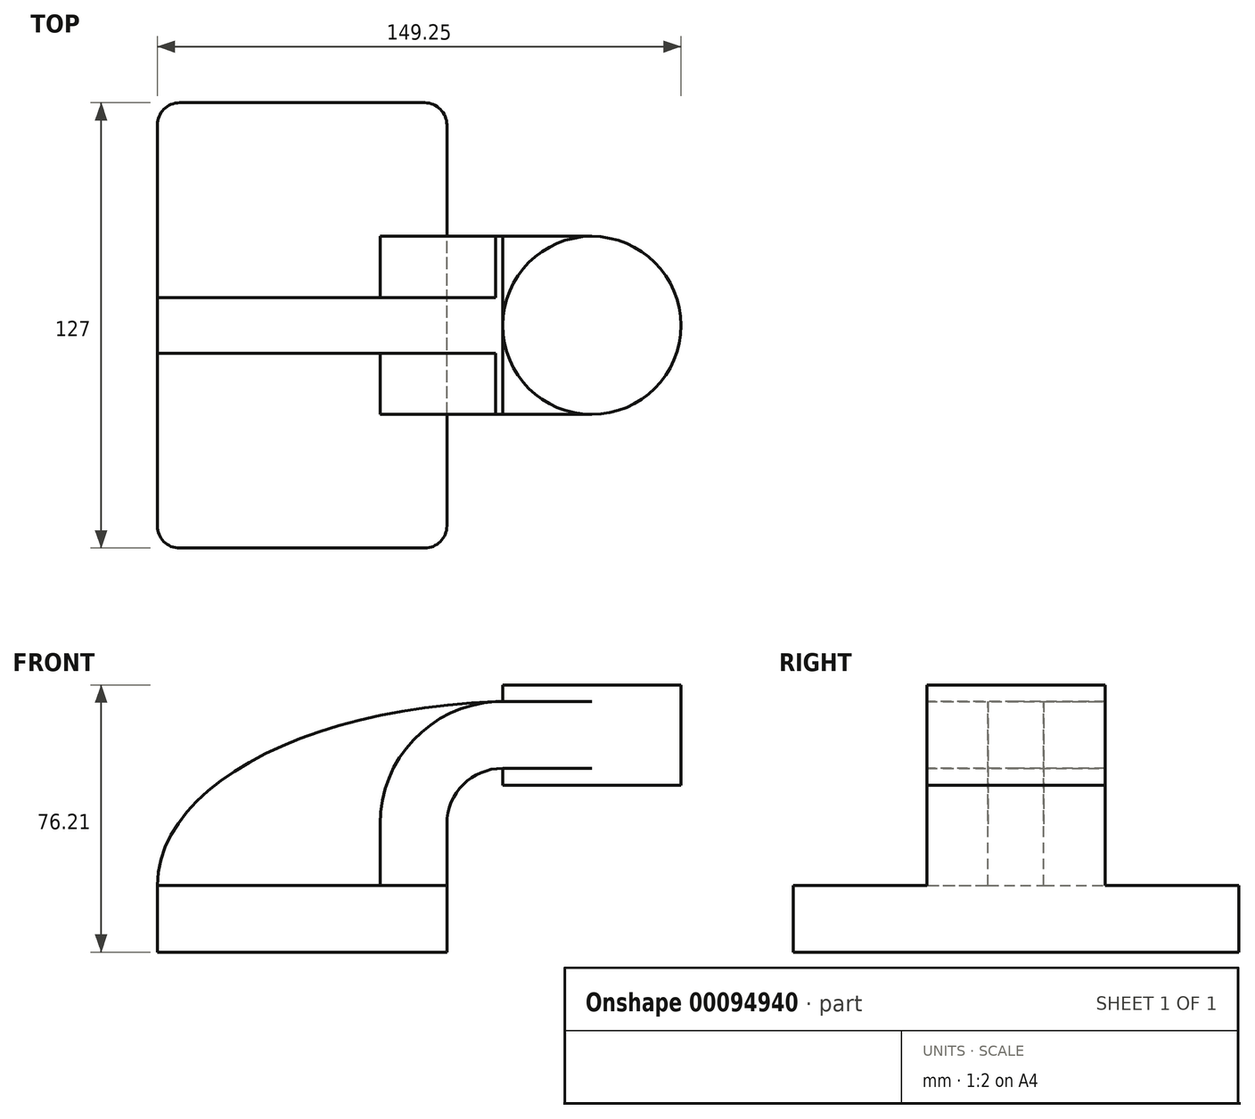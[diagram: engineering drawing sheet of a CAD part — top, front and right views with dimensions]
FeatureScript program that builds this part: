
annotation { "Feature Type Name" : "Feature", "Feature Type Description" : "" }
export const myFeature = defineFeature(function(context is Context, id is Id, definition is map)
    precondition{}
    {
        {
            var Q0;
            Q0=qCreatedBy(makeId("Front.planeOp"),FACE);
            var sketch = newSketch(context, id + "F0", { "sketchPlane" : qUnion([Q0])});
            skLineSegment(sketch, "E0.bottom", {"start": v(41.27, 9.53) * mm, "end": v(-41.28, 9.53) * mm});
            skLineSegment(sketch, "E0.top", {"start": v(41.28, -9.52) * mm, "end": v(-41.27, -9.52) * mm});
            skLineSegment(sketch, "E0.left", {"start": v(41.27, 9.53) * mm, "end": v(41.28, -9.52) * mm});
            skLineSegment(sketch, "E0.right", {"start": v(-41.28, 9.53) * mm, "end": v(-41.27, -9.52) * mm});
            skPoint(sketch, "E0.middle", {"position": v(0, 0) * mm});
            skLineSegment(sketch, "E1.bottom", {"start": v(107.97, 38.1) * mm, "end": v(57.17, 38.1) * mm});
            skLineSegment(sketch, "E1.top", {"start": v(107.97, 66.68) * mm, "end": v(57.17, 66.68) * mm});
            skLineSegment(sketch, "E1.left", {"start": v(107.97, 38.1) * mm, "end": v(107.97, 66.68) * mm});
            skLineSegment(sketch, "E1.right", {"start": v(57.17, 38.1) * mm, "end": v(57.17, 66.68) * mm});
            skPoint(sketch, "E1.middle", {"position": v(82.57, 52.39) * mm});
            skLineSegment(sketch, "E2", {"start": v(41.27, 9.53) * mm, "end": v(41.27, 27) * mm});
            skArc(sketch, "E3", {"start": v(41.27, 27) * mm, "mid": v(45.92, 38.23) * mm, "end": v(57.15, 42.88) * mm});
            skLineSegment(sketch, "E4", {"start": v(57.15, 42.88) * mm, "end": v(82.57, 42.88) * mm});
            skLineSegment(sketch, "E5.0", {"start": v(57.15, 61.93) * mm, "end": v(82.57, 61.93) * mm});
            skArc(sketch, "E5.1", {"start": v(22.22, 27) * mm, "mid": v(32.45, 51.7) * mm, "end": v(57.15, 61.93) * mm});
            skLineSegment(sketch, "E5.2", {"start": v(22.22, 9.53) * mm, "end": v(22.22, 27) * mm});
            skLineSegment(sketch, "E6", {"start": v(82.57, 38.1) * mm, "end": v(82.57, 66.68) * mm});
            skFitSpline(sketch, "E7", {"points": [v(-41.28, 9.53) * mm, v(57.15, 61.93) * mm], "startDerivative": vector(1.14, 87.46) * mm, "endDerivative": vector(161.83, 3.93) * mm});
            skSolve(sketch);
        }
        {
            var Q0;
            Q0=makeQuery(id+"F0.imprint","IMPRINT",FACE,{"disambiguationData":[TD([[makeQuery(id+"F0.imprint","IMPRINT",EDGE,{"derivedFrom":sQuery(id+"F0.wireOp",EDGE,"E0.top")}),-1.0]])]});
            extrude(context, id + "F1", {"entities" : qUnion([Q0]), "endBound" : BoundingType.SYMMETRIC, "depth" : 127 * mm});
        }
        {
            var Q0;
            {var subQ1=sQuery(id+"F0.wireOp",EDGE,"E2");Q0=makeQuery(id+"F0.imprint","IMPRINT",FACE,{"disambiguationData":[TD([[makeQuery(id+"F0.imprint","IMPRINT",EDGE,{"derivedFrom":subQ1}),1.0]])]});}
            var Q1;
            {var subQ0=sQuery(id+"F0.wireOp",EDGE,"E4");var subQ1=sQuery(id+"F0.wireOp",EDGE,"E1.right");var subQ2=makeQuery(id+"F0.imprint","INTERSECT",VERTEX,{"derivedFrom":[subQ1,subQ0]});Q1=makeQuery(id+"F0.imprint","IMPRINT",FACE,{"disambiguationData":[TD([[makeQuery(id+"F0.imprint","IMPRINT",EDGE,{"disambiguationData":[TD([[subQ2,-1.0]])],"derivedFrom":subQ1}),-1.0]])]});}
            extrude(context, id + "F2", {"entities" : qUnion([Q0, Q1]), "operationType" : NewBodyOperationType.ADD, "endBound" : BoundingType.SYMMETRIC, "depth" : 50.8 * mm});
        }
        {
            var Q0;
            {var subQ3=sQuery(id+"F0.wireOp",EDGE,"E5.2");Q0=makeQuery(id+"F0.imprint","IMPRINT",FACE,{"disambiguationData":[TD([[makeQuery(id+"F0.imprint","IMPRINT",EDGE,{"derivedFrom":subQ3}),1.0]])]});}
            extrude(context, id + "F3", {"entities" : qUnion([Q0]), "operationType" : NewBodyOperationType.ADD, "endBound" : BoundingType.SYMMETRIC, "depth" : 15.88 * mm});
        }
        {
            var Q0;
            {var subQ0=sQuery(id+"F0.wireOp",EDGE,"E1.left");Q0=makeQuery(id+"F0.imprint","IMPRINT",FACE,{"disambiguationData":[TD([[makeQuery(id+"F0.imprint","IMPRINT",EDGE,{"derivedFrom":subQ0}),1.0]])]});}
            var Q1;
            Q1=sQuery(id+"F0.wireOp",EDGE,"E6");
            revolve(context, id + "F4", {"operationType" : NewBodyOperationType.ADD, "entities" : qUnion([Q0]), "axis" : qUnion([Q1]), "revolveType" : RevolveType.FULL});
        }
        {
            var Q0;
            Q0=makeQuery(id+"F1.opExtrude","CAP_EDGE",EDGE,{"disambiguationData":[OSD([sQuery(id+"F0.wireOp",EDGE,"E0.right")])],"isStart":false});
            var Q1;
            Q1=makeQuery(id+"F1.opExtrude","CAP_EDGE",EDGE,{"disambiguationData":[OSD([sQuery(id+"F0.wireOp",EDGE,"E0.left")])],"isStart":false});
            var Q2;
            Q2=makeQuery(id+"F1.opExtrude","CAP_EDGE",EDGE,{"disambiguationData":[OSD([sQuery(id+"F0.wireOp",EDGE,"E0.left")])],"isStart":true});
            var Q3;
            Q3=makeQuery(id+"F1.opExtrude","CAP_EDGE",EDGE,{"disambiguationData":[OSD([sQuery(id+"F0.wireOp",EDGE,"E0.right")])],"isStart":true});
            fillet(context, id + "F5", {"entities" : qUnion([Q0, Q1, Q2, Q3]), "radius" : 6.35 * mm, "tangentPropagation" : true, "allowEdgeOverflow" : false});
        }
    });
